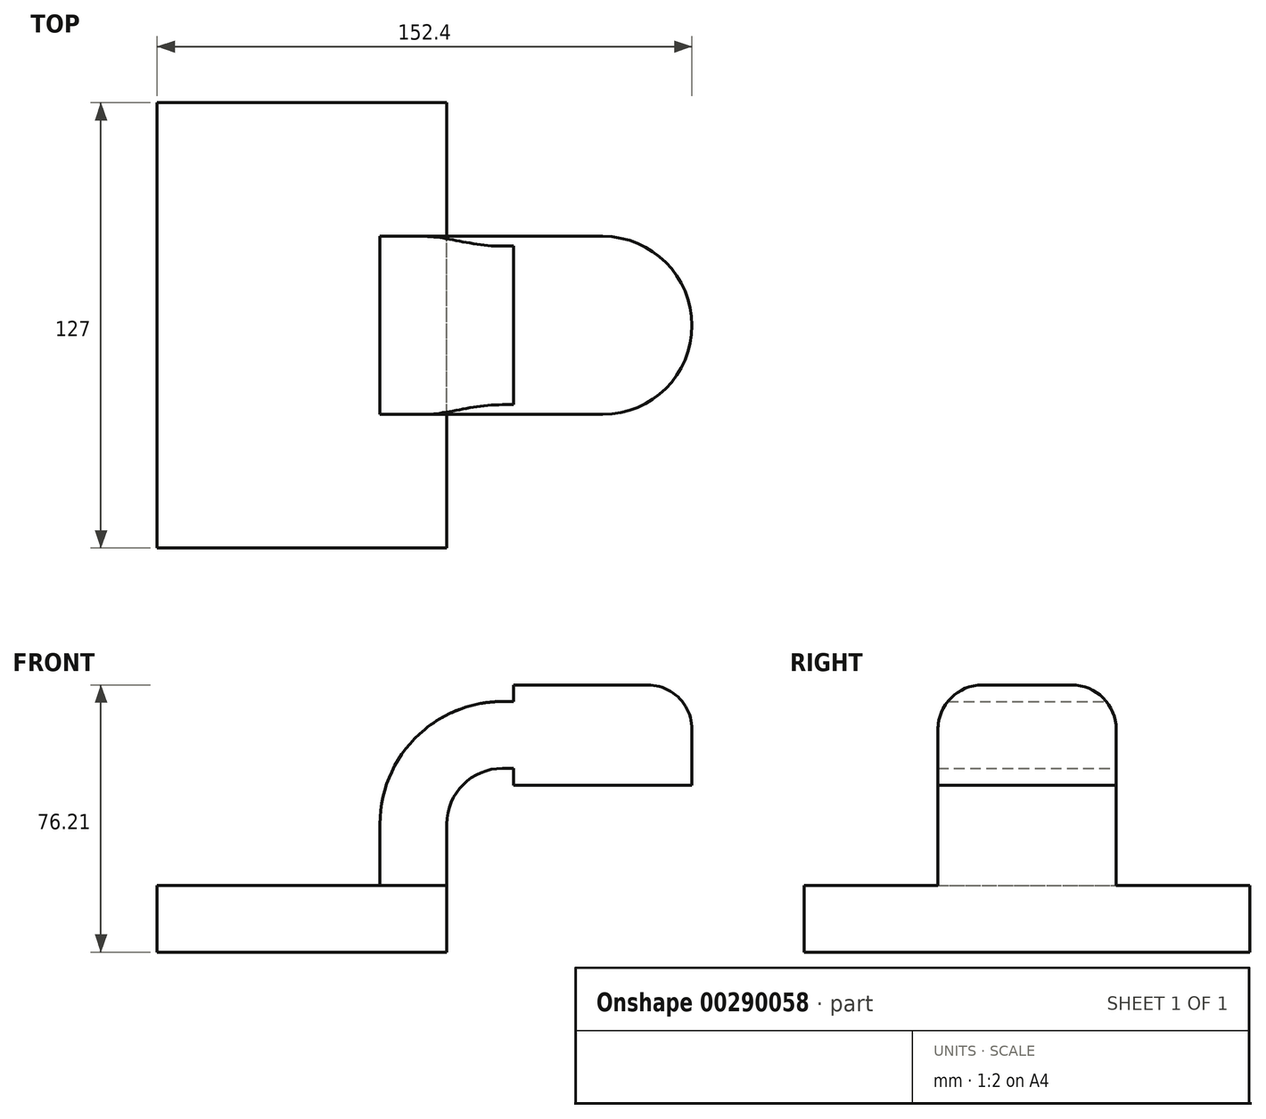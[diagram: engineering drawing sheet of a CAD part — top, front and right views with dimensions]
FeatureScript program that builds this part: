
annotation { "Feature Type Name" : "Feature", "Feature Type Description" : "" }
export const myFeature = defineFeature(function(context is Context, id is Id, definition is map)
    precondition{}
    {
        {
            var Q0;
            Q0=qCreatedBy(makeId("Front.planeOp"),FACE);
            var sketch = newSketch(context, id + "F0", { "sketchPlane" : qUnion([Q0])});
            skLineSegment(sketch, "E0.bottom", {"start": v(41.28, -9.52) * mm, "end": v(-41.28, -9.53) * mm});
            skLineSegment(sketch, "E0.top", {"start": v(41.28, 9.53) * mm, "end": v(-41.28, 9.52) * mm});
            skLineSegment(sketch, "E0.left", {"start": v(41.28, -9.52) * mm, "end": v(41.28, 9.53) * mm});
            skLineSegment(sketch, "E0.right", {"start": v(-41.28, -9.52) * mm, "end": v(-41.28, 9.52) * mm});
            skPoint(sketch, "E0.middle", {"position": v(0, 0) * mm});
            skLineSegment(sketch, "E1.bottom", {"start": v(111.12, 38.1) * mm, "end": v(60.33, 38.1) * mm});
            skLineSegment(sketch, "E1.top", {"start": v(111.13, 66.68) * mm, "end": v(60.33, 66.68) * mm});
            skLineSegment(sketch, "E1.left", {"start": v(111.12, 38.1) * mm, "end": v(111.12, 66.68) * mm});
            skLineSegment(sketch, "E1.right", {"start": v(60.33, 38.1) * mm, "end": v(60.33, 66.68) * mm});
            skPoint(sketch, "E1.middle", {"position": v(85.72, 52.39) * mm});
            skLineSegment(sketch, "E2", {"start": v(41.28, 9.53) * mm, "end": v(41.28, 27) * mm});
            skArc(sketch, "E3", {"start": v(41.28, 27) * mm, "mid": v(45.92, 38.23) * mm, "end": v(57.15, 42.88) * mm});
            skLineSegment(sketch, "E4", {"start": v(57.15, 42.88) * mm, "end": v(85.73, 42.88) * mm});
            skLineSegment(sketch, "E5.0", {"start": v(57.15, 61.93) * mm, "end": v(85.73, 61.93) * mm});
            skArc(sketch, "E5.1", {"start": v(22.23, 27) * mm, "mid": v(32.45, 51.7) * mm, "end": v(57.15, 61.93) * mm});
            skLineSegment(sketch, "E5.2", {"start": v(22.23, 9.53) * mm, "end": v(22.23, 27) * mm});
            skLineSegment(sketch, "E6", {"start": v(85.72, 38.1) * mm, "end": v(85.72, 66.68) * mm});
            skFitSpline(sketch, "E7", {"points": [v(-41.28, 9.52) * mm, v(57.15, 61.93) * mm], "startDerivative": vector(-3.24, 141.52) * mm, "endDerivative": vector(158.94, -0.74) * mm});
            skSolve(sketch);
        }
        {
            var Q0;
            Q0=makeQuery(id+"F0.imprint","IMPRINT",FACE,{"disambiguationData":[TD([[makeQuery(id+"F0.imprint","IMPRINT",EDGE,{"derivedFrom":sQuery(id+"F0.wireOp",EDGE,"E0.bottom")}),-1.0]])]});
            extrude(context, id + "F1", {"entities" : qUnion([Q0]), "endBound" : BoundingType.SYMMETRIC, "depth" : 127 * mm});
        }
        {
            var Q0;
            {var subQ1=sQuery(id+"F0.wireOp",EDGE,"E2");Q0=makeQuery(id+"F0.imprint","IMPRINT",FACE,{"disambiguationData":[TD([[makeQuery(id+"F0.imprint","IMPRINT",EDGE,{"derivedFrom":subQ1}),1.0]])]});}
            var Q1;
            {var subQ0=sQuery(id+"F0.wireOp",EDGE,"E4");var subQ1=sQuery(id+"F0.wireOp",EDGE,"E1.right");var subQ2=makeQuery(id+"F0.imprint","INTERSECT",VERTEX,{"derivedFrom":[subQ1,subQ0]});Q1=makeQuery(id+"F0.imprint","IMPRINT",FACE,{"disambiguationData":[TD([[makeQuery(id+"F0.imprint","IMPRINT",EDGE,{"disambiguationData":[TD([[subQ2,-1.0]])],"derivedFrom":subQ1}),-1.0]])]});}
            var Q2;
            {var subQ0=sQuery(id+"F0.wireOp",EDGE,"E1.right");var subQ1=sQuery(id+"F0.wireOp",EDGE,"E1.bottom");var subQ2=makeQuery(id+"F0.imprint","INTERSECT",VERTEX,{"derivedFrom":[subQ1,subQ0]});Q2=makeQuery(id+"F0.imprint","IMPRINT",FACE,{"disambiguationData":[TD([[makeQuery(id+"F0.imprint","IMPRINT",EDGE,{"disambiguationData":[TD([[subQ2,1.0]])],"derivedFrom":subQ1}),-1.0]])]});}
            var Q3;
            {var subQ0=sQuery(id+"F0.wireOp",EDGE,"E1.right");var subQ1=sQuery(id+"F0.wireOp",EDGE,"E1.top");var subQ2=makeQuery(id+"F0.imprint","INTERSECT",VERTEX,{"derivedFrom":[subQ1,subQ0]});Q3=makeQuery(id+"F0.imprint","IMPRINT",FACE,{"disambiguationData":[TD([[makeQuery(id+"F0.imprint","IMPRINT",EDGE,{"disambiguationData":[TD([[subQ2,1.0]])],"derivedFrom":subQ1}),1.0]])]});}
            extrude(context, id + "F2", {"entities" : qUnion([Q0, Q1, Q2, Q3]), "operationType" : NewBodyOperationType.ADD, "endBound" : BoundingType.SYMMETRIC, "depth" : 50.8 * mm});
        }
        {
            var Q0;
            {var subQ4=sQuery(id+"F0.wireOp",EDGE,"E1.left");Q0=makeQuery(id+"F0.imprint","IMPRINT",FACE,{"disambiguationData":[TD([[makeQuery(id+"F0.imprint","IMPRINT",EDGE,{"derivedFrom":subQ4}),1.0]])]});}
            var Q1;
            Q1=sQuery(id+"F0.wireOp",EDGE,"E6");
            revolve(context, id + "F3", {"operationType" : NewBodyOperationType.ADD, "entities" : qUnion([Q0]), "axis" : qUnion([Q1]), "revolveType" : RevolveType.FULL});
        }
        {
            var Q0;
            Q0=makeQuery(id+"F0.imprint","IMPRINT",FACE,{"disambiguationData":[TD([[makeQuery(id+"F0.imprint","IMPRINT",EDGE,{"derivedFrom":sQuery(id+"F0.wireOp",EDGE,"E5.1")}),1.0]])]});
            extrude(context, id + "F4", {"entities" : qUnion([Q0]), "operationType" : NewBodyOperationType.ADD, "endBound" : BoundingType.SYMMETRIC, "depth" : 6.35 * mm});
        }
        {
            var Q0;
            Q0=makeQuery(id+"F3.opRevolve","SWEPT_EDGE",EDGE,{"disambiguationData":[OSD([sQuery(id+"F0.wireOp",EDGE,"E1.top"),sQuery(id+"F0.wireOp",EDGE,"E1.left")])]});
            fillet(context, id + "F5", {"entities" : qUnion([Q0]), "radius" : 12.7 * mm, "tangentPropagation" : true, "allowEdgeOverflow" : false});
        }
    });
